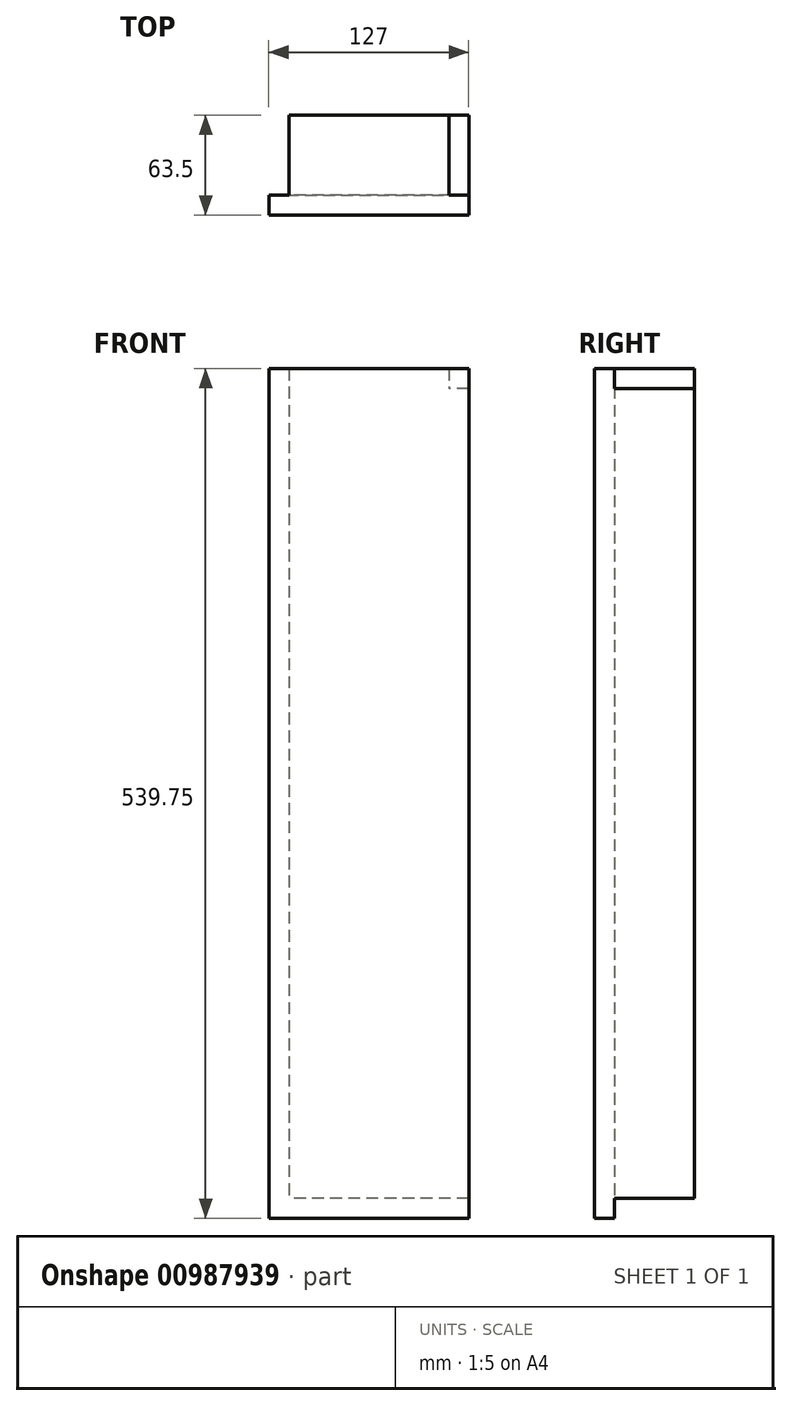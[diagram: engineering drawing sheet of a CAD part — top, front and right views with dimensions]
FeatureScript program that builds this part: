
annotation { "Feature Type Name" : "Feature", "Feature Type Description" : "" }
export const myFeature = defineFeature(function(context is Context, id is Id, definition is map)
    precondition{}
    {
        {
            var Q0;
            Q0=qCreatedBy(makeId("Front.planeOp"),FACE);
            var sketch = newSketch(context, id + "F0", { "sketchPlane" : qUnion([Q0])});
            skLineSegment(sketch, "E0.bottom", {"start": v(-35.86, 493.2) * mm, "end": v(91.14, 493.2) * mm});
            skLineSegment(sketch, "E0.top", {"start": v(-35.86, -46.55) * mm, "end": v(91.14, -46.55) * mm});
            skLineSegment(sketch, "E0.left", {"start": v(-35.86, 493.2) * mm, "end": v(-35.86, -46.55) * mm});
            skLineSegment(sketch, "E0.right", {"start": v(91.14, 493.2) * mm, "end": v(91.14, -46.55) * mm});
            skSolve(sketch);
        }
        {
            var Q0;
            Q0=makeQuery(id+"F0.imprint","IMPRINT",FACE,{"disambiguationData":[TD([[makeQuery(id+"F0.imprint","IMPRINT",EDGE,{"derivedFrom":sQuery(id+"F0.wireOp",EDGE,"E0.bottom")}),-1.0]])]});
            extrude(context, id + "F1", {"entities" : qUnion([Q0]), "depth" : 12.7 * mm, "offsetDistance" : 25.4 * mm});
        }
        {
            var Q0;
            Q0=makeQuery(id+"F1.opExtrude","CAP_FACE",FACE,{"disambiguationData":[OSD([sQuery(id+"F0.wireOp",EDGE,"E0.bottom"),sQuery(id+"F0.wireOp",EDGE,"E0.top"),sQuery(id+"F0.wireOp",EDGE,"E0.left"),sQuery(id+"F0.wireOp",EDGE,"E0.right")])],"isStart":true});
            var sketch = newSketch(context, id + "F2", { "sketchPlane" : qUnion([Q0])});
            skLineSegment(sketch, "E1.bottom", {"start": v(-91.14, 493.2) * mm, "end": v(35.86, 493.2) * mm});
            skLineSegment(sketch, "E1.top", {"start": v(-91.14, -46.55) * mm, "end": v(35.86, -46.55) * mm});
            skLineSegment(sketch, "E1.left", {"start": v(-91.14, 493.2) * mm, "end": v(-91.14, -46.55) * mm});
            skLineSegment(sketch, "E1.right", {"start": v(35.86, 493.2) * mm, "end": v(35.86, -46.55) * mm});
            skLineSegment(sketch, "E2", {"start": v(-61.54, 493.2) * mm, "end": v(-61.54, 480.5) * mm});
            skLineSegment(sketch, "E3.top", {"start": v(-91.14, 480.5) * mm, "end": v(35.86, 480.5) * mm});
            skLineSegment(sketch, "E3.left", {"start": v(-91.14, 493.2) * mm, "end": v(-91.14, 480.5) * mm});
            skLineSegment(sketch, "E3.right", {"start": v(35.86, 493.2) * mm, "end": v(35.86, 480.5) * mm});
            skLineSegment(sketch, "E4.top", {"start": v(-91.14, -33.85) * mm, "end": v(35.86, -33.85) * mm});
            skLineSegment(sketch, "E4.left", {"start": v(-91.14, -46.55) * mm, "end": v(-91.14, -33.85) * mm});
            skLineSegment(sketch, "E4.right", {"start": v(35.86, -46.55) * mm, "end": v(35.86, -33.85) * mm});
            skLineSegment(sketch, "E5.bottom", {"start": v(-91.14, 493.2) * mm, "end": v(-78.44, 493.2) * mm});
            skLineSegment(sketch, "E5.top", {"start": v(-91.14, -46.55) * mm, "end": v(-78.44, -46.55) * mm});
            skLineSegment(sketch, "E5.right", {"start": v(-78.44, 493.2) * mm, "end": v(-78.44, -46.55) * mm});
            skLineSegment(sketch, "E6.bottom", {"start": v(35.86, 493.2) * mm, "end": v(23.16, 493.2) * mm});
            skLineSegment(sketch, "E6.top", {"start": v(35.86, -46.55) * mm, "end": v(23.16, -46.55) * mm});
            skLineSegment(sketch, "E6.right", {"start": v(23.16, 493.2) * mm, "end": v(23.16, -46.55) * mm});
            skSolve(sketch);
        }
        {
            var Q0;
            {var subQ0=sQuery(id+"F2.wireOp",EDGE,"E1.left");var subQ1=sQuery(id+"F2.wireOp",EDGE,"E3.top");var subQ2=makeQuery(id+"F2.imprint","INTERSECT",VERTEX,{"derivedFrom":[subQ1,subQ0]});Q0=makeQuery(id+"F2.imprint","IMPRINT",FACE,{"disambiguationData":[TD([[makeQuery(id+"F2.imprint","IMPRINT",EDGE,{"disambiguationData":[TD([[subQ2,-1.0]])],"derivedFrom":subQ1}),-1.0]])]});}
            var Q1;
            {var subQ5=sQuery(id+"F2.wireOp",EDGE,"E5.bottom");Q1=makeQuery(id+"F2.imprint","IMPRINT",FACE,{"disambiguationData":[TD([[makeQuery(id+"F2.imprint","IMPRINT",EDGE,{"derivedFrom":subQ5}),1.0]])]});}
            var Q2;
            {var subQ0=sQuery(id+"F2.wireOp",EDGE,"E2");Q2=makeQuery(id+"F2.imprint","IMPRINT",FACE,{"disambiguationData":[TD([[makeQuery(id+"F2.imprint","IMPRINT",EDGE,{"derivedFrom":subQ0}),-1.0]])]});}
            var Q3;
            {var subQ0=sQuery(id+"F2.wireOp",EDGE,"E2");Q3=makeQuery(id+"F2.imprint","IMPRINT",FACE,{"disambiguationData":[TD([[makeQuery(id+"F2.imprint","IMPRINT",EDGE,{"derivedFrom":subQ0}),1.0]])]});}
            var Q4;
            {var subQ5=sQuery(id+"F2.wireOp",EDGE,"E6.bottom");Q4=makeQuery(id+"F2.imprint","IMPRINT",FACE,{"disambiguationData":[TD([[makeQuery(id+"F2.imprint","IMPRINT",EDGE,{"derivedFrom":subQ5}),1.0]])]});}
            var Q5;
            {var subQ0=sQuery(id+"F2.wireOp",EDGE,"E1.right");var subQ1=sQuery(id+"F2.wireOp",EDGE,"E3.top");var subQ2=makeQuery(id+"F2.imprint","INTERSECT",VERTEX,{"derivedFrom":[subQ1,subQ0]});Q5=makeQuery(id+"F2.imprint","IMPRINT",FACE,{"disambiguationData":[TD([[makeQuery(id+"F2.imprint","IMPRINT",EDGE,{"disambiguationData":[TD([[subQ2,1.0]])],"derivedFrom":subQ1}),-1.0]])]});}
            var Q6;
            {var subQ5=sQuery(id+"F2.wireOp",EDGE,"E6.top");Q6=makeQuery(id+"F2.imprint","IMPRINT",FACE,{"disambiguationData":[TD([[makeQuery(id+"F2.imprint","IMPRINT",EDGE,{"derivedFrom":subQ5}),-1.0]])]});}
            var Q7;
            {var subQ0=sQuery(id+"F2.wireOp",EDGE,"E1.top");Q7=makeQuery(id+"F2.imprint","IMPRINT",FACE,{"disambiguationData":[TD([[makeQuery(id+"F2.imprint","IMPRINT",EDGE,{"derivedFrom":subQ0}),-1.0]])]});}
            var Q8;
            {var subQ5=sQuery(id+"F2.wireOp",EDGE,"E5.top");Q8=makeQuery(id+"F2.imprint","IMPRINT",FACE,{"disambiguationData":[TD([[makeQuery(id+"F2.imprint","IMPRINT",EDGE,{"derivedFrom":subQ5}),-1.0]])]});}
            extrude(context, id + "F3", {"entities" : qUnion([Q0, Q1, Q2, Q3, Q4, Q5, Q6, Q7, Q8]), "operationType" : NewBodyOperationType.ADD, "depth" : 50.8 * mm, "offsetDistance" : 25.4 * mm});
        }
    });
